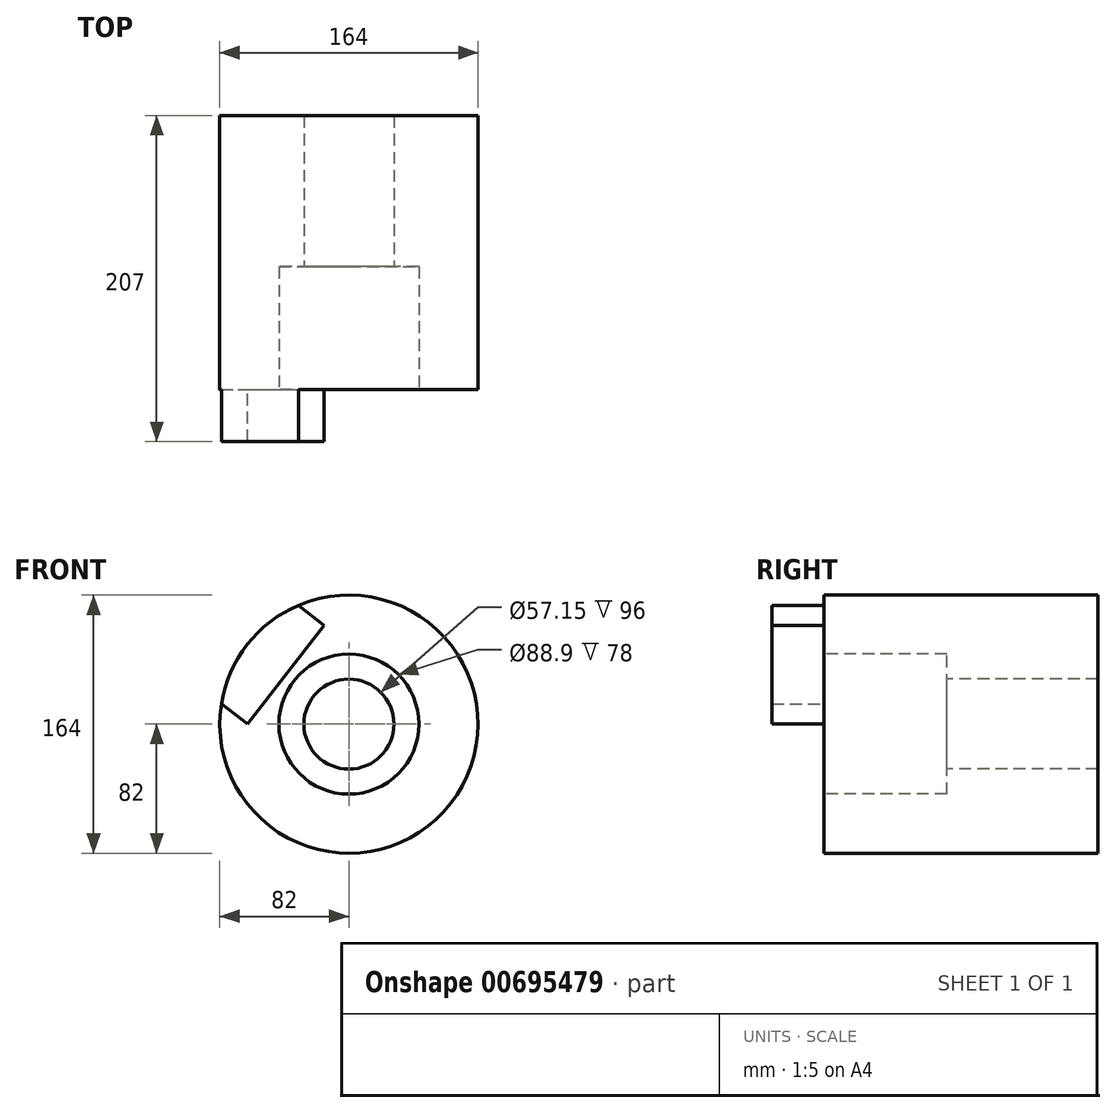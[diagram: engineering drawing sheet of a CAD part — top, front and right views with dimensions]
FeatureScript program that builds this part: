
annotation { "Feature Type Name" : "Feature", "Feature Type Description" : "" }
export const myFeature = defineFeature(function(context is Context, id is Id, definition is map)
    precondition{}
    {
        {
            var Q0;
            Q0=qCreatedBy(makeId("Front.planeOp"),FACE);
            var sketch = newSketch(context, id + "F0", { "sketchPlane" : qUnion([Q0])});
            skCircle(sketch, "E0", {"center": v(0, 0) * mm, "radius": 82 * mm});
            skSolve(sketch);
        }
        {
            var Q0;
            Q0=makeQuery(id+"F0.imprint","IMPRINT",FACE,{"disambiguationData":[TD([[makeQuery(id+"F0.imprint","IMPRINT",EDGE,{"derivedFrom":sQuery(id+"F0.wireOp",EDGE,"E0")}),1.0]])]});
            extrude(context, id + "F1", {"entities" : qUnion([Q0]), "depth" : 25 * mm, "offsetDistance" : 25 * mm, "hasSecondDirection" : true, "secondDirectionOppositeDirection" : true, "secondDirectionDepth" : 149 * mm});
        }
        {
            var Q0;
            Q0=makeQuery(id+"F1.opExtrude","CAP_FACE",FACE,{"disambiguationData":[OSD([sQuery(id+"F0.wireOp",EDGE,"E0")])],"isStart":false});
            var sketch = newSketch(context, id + "F2", { "sketchPlane" : qUnion([Q0])});
            skCircle(sketch, "E1", {"center": v(0, 0) * mm, "radius": 28.57 * mm});
            skSolve(sketch);
        }
        {
            var Q0;
            Q0=makeQuery(id+"F2.imprint","IMPRINT",FACE,{"disambiguationData":[TD([[makeQuery(id+"F2.imprint","IMPRINT",EDGE,{"derivedFrom":sQuery(id+"F2.wireOp",EDGE,"E1")}),1.0]])]});
            extrude(context, id + "F3", {"entities" : qUnion([Q0]), "operationType" : NewBodyOperationType.REMOVE, "endBound" : BoundingType.THROUGH_ALL, "oppositeDirection" : true, "depth" : 25 * mm, "offsetDistance" : 25 * mm});
        }
        {
            var Q0;
            Q0=makeQuery(id+"F1.opExtrude","CAP_FACE",FACE,{"disambiguationData":[OSD([sQuery(id+"F0.wireOp",EDGE,"E0")])],"isStart":false});
            var sketch = newSketch(context, id + "F4", { "sketchPlane" : qUnion([Q0])});
            skLineSegment(sketch, "E2", {"start": v(0, 0) * mm, "end": v(-64.62, 50.48) * mm, "construction": true});
            skPoint(sketch, "E3", {"position": v(-32.1, 75.46) * mm});
            skPoint(sketch, "E4", {"position": v(-80.98, 12.9) * mm});
            skLineSegment(sketch, "E5", {"start": v(-80.98, 12.9) * mm, "end": v(-64.48, 0) * mm});
            skLineSegment(sketch, "E6", {"start": v(-32.1, 75.46) * mm, "end": v(-15.9, 62.8) * mm});
            skLineSegment(sketch, "E7", {"start": v(-64.48, 0) * mm, "end": v(-15.9, 62.8) * mm});
            skArc(sketch, "E8", {"start": v(-32.1, 75.46) * mm, "mid": v(-64.62, 50.48) * mm, "end": v(-80.98, 12.9) * mm});
            skSolve(sketch);
        }
        {
            var Q0;
            {var subQ1=sQuery(id+"F4.wireOp",EDGE,"E5");Q0=makeQuery(id+"F4.imprint","IMPRINT",FACE,{"disambiguationData":[TD([[makeQuery(id+"F4.imprint","IMPRINT",EDGE,{"derivedFrom":subQ1}),-1.0]])]});}
            var sketch = newSketch(context, id + "F5", { "sketchPlane" : qUnion([Q0])});
            skSolve(sketch);
        }
        {
            var Q0;
            Q0=makeQuery(id+"F4.imprint","IMPRINT",FACE,{"disambiguationData":[TD([[makeQuery(id+"F4.imprint","IMPRINT",EDGE,{"derivedFrom":sQuery(id+"F4.wireOp",EDGE,"E5")}),1.0]])]});
            extrude(context, id + "F6", {"entities" : qUnion([Q0]), "operationType" : NewBodyOperationType.ADD, "depth" : 33 * mm, "offsetDistance" : 25 * mm});
        }
        {
            var Q0;
            {var subQ1=sQuery(id+"F4.wireOp",EDGE,"E5");Q0=makeQuery(id+"F5.imprint","IMPRINT",FACE,{"disambiguationData":[TD([[makeQuery(id+"F5.imprint","IMPRINT",EDGE,{"derivedFrom":makeQuery(id+"F4.imprint","IMPRINT",EDGE,{"derivedFrom":subQ1})}),-1.0]])]});}
            var sketch = newSketch(context, id + "F7", { "sketchPlane" : qUnion([Q0])});
            skCircle(sketch, "E9", {"center": v(0, 0) * mm, "radius": 44.45 * mm});
            skSolve(sketch);
        }
        {
            var Q0;
            Q0=makeQuery(id+"F7.imprint","IMPRINT",FACE,{"disambiguationData":[TD([[makeQuery(id+"F7.imprint","IMPRINT",EDGE,{"derivedFrom":sQuery(id+"F7.wireOp",EDGE,"E9")}),1.0]])]});
            extrude(context, id + "F8", {"entities" : qUnion([Q0]), "operationType" : NewBodyOperationType.REMOVE, "oppositeDirection" : true, "depth" : 78 * mm, "offsetDistance" : 25 * mm});
        }
        {
            var Q0;
            {var subQ1=sQuery(id+"F4.wireOp",EDGE,"E5");Q0=makeQuery(id+"F5.imprint","IMPRINT",FACE,{"disambiguationData":[TD([[makeQuery(id+"F5.imprint","IMPRINT",EDGE,{"derivedFrom":makeQuery(id+"F4.imprint","IMPRINT",EDGE,{"derivedFrom":subQ1})}),-1.0]])]});}
            var sketch = newSketch(context, id + "F9", { "sketchPlane" : qUnion([Q0])});
            skLineSegment(sketch, "E10", {"start": v(0, 95.25) * mm, "end": v(0, 0) * mm});
            skLineSegment(sketch, "E11", {"start": v(0, 0) * mm, "end": v(-10, 0) * mm});
            skLineSegment(sketch, "E12", {"start": v(-10, 0) * mm, "end": v(-10, -94.12) * mm});
            skLineSegment(sketch, "E13", {"start": v(91, -94.12) * mm, "end": v(91, 95.25) * mm});
            skLineSegment(sketch, "E14", {"start": v(-10, -94.12) * mm, "end": v(91, -94.12) * mm});
            skLineSegment(sketch, "E15", {"start": v(91, 95.25) * mm, "end": v(0, 95.25) * mm});
            skSolve(sketch);
        }
        {
            var Q0;
            Q0=makeQuery(id+"F9.imprint","IMPRINT",FACE,{"disambiguationData":[TD([[makeQuery(id+"F9.imprint","IMPRINT",EDGE,{"derivedFrom":sQuery(id+"F9.wireOp",EDGE,"E13")}),1.0]])]});
            var Q1;
            {var subQ0=sQuery(id+"F9.wireOp",EDGE,"E10");var subQ5=makeQuery(id+"F5.imprint","IMPRINT",EDGE,{"derivedFrom":makeQuery(id+"F4.imprint","IMPRINT",EDGE,{"derivedFrom":makeQuery(id+"F3.boolean.opBoolean","COPY",EDGE,{"derivedFrom":makeQuery(id+"F3.opExtrude","CAP_EDGE",EDGE,{"disambiguationData":[OSD([sQuery(id+"F2.wireOp",EDGE,"E1")])],"isStart":true})})})});var subQ6=makeQuery(id+"F9.imprint","INTERSECT",VERTEX,{"derivedFrom":[subQ5,subQ0]});Q1=makeQuery(id+"F9.imprint","IMPRINT",FACE,{"disambiguationData":[TD([[makeQuery(id+"F9.imprint","IMPRINT",EDGE,{"disambiguationData":[TD([[subQ6,1.0]])],"derivedFrom":subQ5}),-1.0]])]});}
            extrude(context, id + "F10", {"entities" : qUnion([Q0, Q1]), "operationType" : NewBodyOperationType.REMOVE, "endBound" : BoundingType.THROUGH_ALL, "oppositeDirection" : true, "depth" : 25 * mm, "offsetDistance" : 25 * mm});
        }
    });
